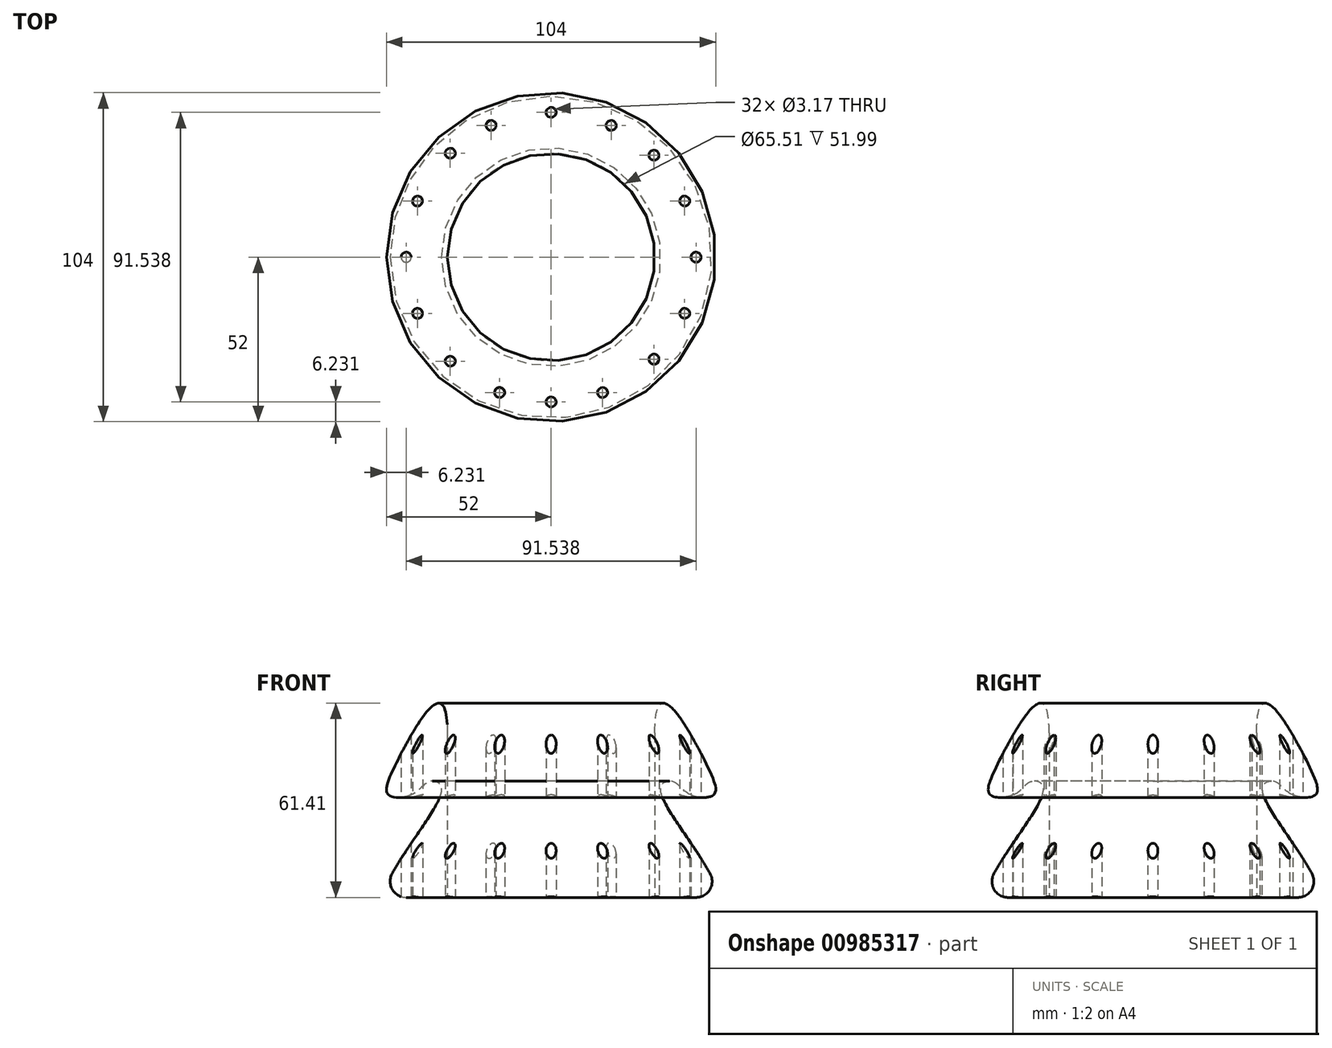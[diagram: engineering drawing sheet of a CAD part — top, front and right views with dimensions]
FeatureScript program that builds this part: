
annotation { "Feature Type Name" : "Feature", "Feature Type Description" : "" }
export const myFeature = defineFeature(function(context is Context, id is Id, definition is map)
    precondition{}
    {
        {
            var Q0;
            Q0=qCreatedBy(makeId("Front.planeOp"),FACE);
            var sketch = newSketch(context, id + "F0", { "sketchPlane" : qUnion([Q0])});
            skFitSpline(sketch, "E0", {"points": [v(-52.87, -44.79) * mm, v(-34.58, -10.46) * mm, v(-38.42, -8.11) * mm, v(-43.33, -11.95) * mm, v(-51.35, -12.33) * mm, v(-49.73, -4.06) * mm, v(-36.84, 17.12) * mm, v(-19.68, 28.43) * mm, v(0, 31.41) * mm], "startDerivative": vector(5.44, 131.41) * mm, "endDerivative": vector(93.25, 1.12) * mm});
            skLineSegment(sketch, "E1", {"start": v(-52.87, -44.79) * mm, "end": v(0, -44.79) * mm});
            skFitSpline(sketch, "E2.MirrorCS", {"points": [v(52.87, -44.79) * mm, v(34.58, -10.46) * mm, v(38.42, -8.11) * mm, v(43.33, -11.95) * mm, v(51.35, -12.33) * mm, v(49.73, -4.06) * mm, v(36.84, 17.12) * mm, v(19.68, 28.43) * mm, v(0, 31.41) * mm], "startDerivative": vector(-5.44, 131.41) * mm, "endDerivative": vector(-93.25, 1.12) * mm});
            skLineSegment(sketch, "E3.MirrorCS", {"start": v(52.87, -44.79) * mm, "end": v(0, -44.79) * mm});
            skLineSegment(sketch, "E4", {"start": v(0, 31.41) * mm, "end": v(0, -44.79) * mm});
            skSolve(sketch);
        }
        {
            var Q0;
            Q0=makeQuery(id+"F0.imprint","IMPRINT",FACE,{"disambiguationData":[TD([[makeQuery(id+"F0.imprint","IMPRINT",EDGE,{"derivedFrom":sQuery(id+"F0.wireOp",EDGE,"E0")}),-1.0]])]});
            var Q1;
            Q1=sQuery(id+"F0.wireOp",EDGE,"E4");
            revolve(context, id + "F1", {"surfaceOperationType" : NewSurfaceOperationType.NEW, "entities" : qUnion([Q0]), "axis" : qUnion([Q1]), "revolveType" : RevolveType.FULL, "oppositeDirection" : true});
        }
        {
            var Q0;
            Q0=qCreatedBy(makeId("Top.planeOp"),FACE);
            var sketch = newSketch(context, id + "F2", { "sketchPlane" : qUnion([Q0])});
            skCircle(sketch, "E5", {"center": v(0, 0) * mm, "radius": 32.75 * mm});
            skSolve(sketch);
        }
        {
            var Q0;
            Q0=qSketchRegion(id+"F2",true);
            var Q1;
            Q1=qSketchRegion(id+"FyJb5VjQGFGTzOf_1",true);
            extrude(context, id + "F3", {"entities" : qUnion([Q0, Q1]), "operationType" : NewBodyOperationType.REMOVE, "endBound" : BoundingType.THROUGH_ALL, "depth" : 30.48 * mm, "offsetDistance" : 25.4 * mm});
        }
        {
            var Q0;
            Q0=makeQuery(id+"F2.imprint","IMPRINT",FACE,{"disambiguationData":[TD([[makeQuery(id+"F2.imprint","IMPRINT",EDGE,{"derivedFrom":sQuery(id+"F2.wireOp",EDGE,"E5")}),1.0]])]});
            extrude(context, id + "F4", {"entities" : qUnion([Q0]), "operationType" : NewBodyOperationType.REMOVE, "endBound" : BoundingType.THROUGH_ALL, "oppositeDirection" : true, "depth" : 77.22 * mm, "offsetDistance" : 25.4 * mm});
        }
        {
            var Q0;
            Q0=makeQuery(id+"F3.boolean.opBoolean","INTERSECT",EDGE,{"derivedFrom":[makeQuery(id+"F1.opRevolve","SWEPT_FACE",FACE,{"disambiguationData":[OSD([sQuery(id+"F0.wireOp",EDGE,"E0")])]}),makeQuery(id+"F3.opExtrude","SWEPT_FACE",FACE,{"disambiguationData":[OSD([sQuery(id+"F2.wireOp",EDGE,"E5")])]})]});
            fillet(context, id + "F5", {"entities" : qUnion([Q0]), "radius" : 5.08 * mm, "tangentPropagation" : true, "rho" : 0.5, "crossSection" : FilletCrossSection.CONIC, "allowEdgeOverflow" : false});
        }
        {
            var Q0;
            Q0=makeQuery(id+"F1.opRevolve","SWEPT_EDGE",EDGE,{"disambiguationData":[OSD([sQuery(id+"F0.wireOp",EDGE,"E0"),sQuery(id+"F0.wireOp",EDGE,"E1")])]});
            fillet(context, id + "F6", {"entities" : qUnion([Q0]), "radius" : 5.08 * mm, "tangentPropagation" : true, "allowEdgeOverflow" : false});
        }
        {
            var Q0;
            Q0=makeQuery(id+"F1.opRevolve","SWEPT_FACE",FACE,{"disambiguationData":[OSD([sQuery(id+"F0.wireOp",EDGE,"E1")])]});
            var sketch = newSketch(context, id + "F7", { "sketchPlane" : qUnion([Q0])});
            skPoint(sketch, "E6", {"position": v(45.77, 0) * mm});
            skPoint(sketch, "E7", {"position": v(-45.77, 0) * mm});
            skPoint(sketch, "E8", {"position": v(0, -45.77) * mm});
            skPoint(sketch, "E9", {"position": v(0, 45.77) * mm});
            skPoint(sketch, "E10", {"position": v(-31.85, 32.87) * mm});
            skPoint(sketch, "E11", {"position": v(-42.18, 17.75) * mm});
            skPoint(sketch, "E12", {"position": v(-31.85, -32.87) * mm});
            skPoint(sketch, "E13", {"position": v(-42.18, -17.75) * mm});
            skPoint(sketch, "E14", {"position": v(-18.97, -41.65) * mm});
            skPoint(sketch, "E15", {"position": v(32.48, -32.24) * mm});
            skPoint(sketch, "E16", {"position": v(18.97, -41.65) * mm});
            skPoint(sketch, "E17", {"position": v(42.18, -17.75) * mm});
            skPoint(sketch, "E18", {"position": v(32.48, 32.24) * mm});
            skPoint(sketch, "E19", {"position": v(42.18, 17.75) * mm});
            skPoint(sketch, "E20", {"position": v(16.25, 42.79) * mm});
            skPoint(sketch, "E21", {"position": v(-16.25, 42.79) * mm});
            skSolve(sketch);
        }
        {
            var Q0;
            Q0=sQuery(id+"F7.wireOp",VERTEX,"E10");
            var Q1;
            Q1=sQuery(id+"F7.wireOp",VERTEX,"E11");
            var Q2;
            Q2=sQuery(id+"F7.wireOp",VERTEX,"E7");
            var Q3;
            Q3=sQuery(id+"F7.wireOp",VERTEX,"E13");
            var Q4;
            Q4=sQuery(id+"F7.wireOp",VERTEX,"E12");
            var Q5;
            Q5=sQuery(id+"F7.wireOp",VERTEX,"E14");
            var Q6;
            Q6=sQuery(id+"F7.wireOp",VERTEX,"E8");
            var Q7;
            Q7=sQuery(id+"F7.wireOp",VERTEX,"E16");
            var Q8;
            Q8=sQuery(id+"F7.wireOp",VERTEX,"E15");
            var Q9;
            Q9=sQuery(id+"F7.wireOp",VERTEX,"E17");
            var Q10;
            Q10=sQuery(id+"F7.wireOp",VERTEX,"E6");
            var Q11;
            Q11=sQuery(id+"F7.wireOp",VERTEX,"E19");
            var Q12;
            Q12=sQuery(id+"F7.wireOp",VERTEX,"E18");
            var Q13;
            Q13=sQuery(id+"F7.wireOp",VERTEX,"E20");
            var Q14;
            Q14=sQuery(id+"F7.wireOp",VERTEX,"E9");
            var Q15;
            Q15=sQuery(id+"F7.wireOp",VERTEX,"E21");
            var Q16;
            Q16=makeQuery(id+"F1.opRevolve","SWEPT_BODY",BODY,{"disambiguationData":[OSD([sQuery(id+"F0.wireOp",EDGE,"E0"),sQuery(id+"F0.wireOp",EDGE,"E1"),sQuery(id+"F0.wireOp",EDGE,"E4")])]});
            hole(context, id + "F8", {"style" : HoleStyle.SIMPLE, "endStyle" : HoleEndStyle.THROUGH, "holeDiameter" : 3.17 * mm, "majorDiameter" : 6.35 * mm, "isTappedThrough" : true, "tappedDepth" : 12.7 * mm, "tapClearance" : 3, "locations" : qUnion([Q0, Q1, Q2, Q3, Q4, Q5, Q6, Q7, Q8, Q9, Q10, Q11, Q12, Q13, Q14, Q15]), "scope" : qUnion([Q16])});
        }
    });
